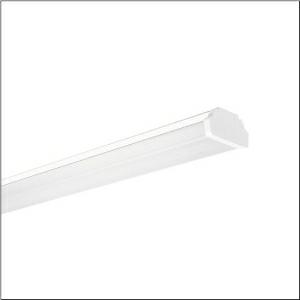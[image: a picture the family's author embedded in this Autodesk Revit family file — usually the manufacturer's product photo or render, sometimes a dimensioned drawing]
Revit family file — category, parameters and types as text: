
# Revit family: dus_r__31_ho_53bd812m1v4120_db1b
name_source: partatom
category: Lighting Fixtures
units: mm (PartAtom-declared; Revit-internal decimal feet)

## family parameters
Cut with Voids When Loaded = No
Host = Face
Light Source = No
Part Type = Normal
Room Calculation Point = No
Round Connector Dimension = Use Diameter
Shared = No

## types (1)
- --- (1 x LED, 12380 lm, 77.3 W, 4000K)
    Apparent Load = 77 VA
    CIE Flux Codes = 47 80 95 92 100
    Color Rendering = 80
    Color Temperature = 4000K
    Default Elevation = 1800 mm
    Description = DUS® 31 HO, luminaire insert, of sheet steel, coil coated, white, length: 1.535mm, width: 81mm, height: 90mm, 5x system unit, system units: 307mm, LED rated luminous flux: 12.380lm, light colour: 840, control gear: ON/OFF Multilumen, control gear: ECG Multilumen, with plug, 3-pole, with phase selection, mains connection: 220..240V, AC, 50/60Hz, rated input power: 77W, through-wiring accessed according to module size, primary optical cover: cover, of PMMA, light emission: direct distribution, primary light characteristic: symmetric, protection rating (complete): IP20, protection rating (LED compartment): IP50, insulation class (complete): insulation class I (protective earthing), certification: CE, ENEC, VDE, UKCA, impact resistance: IK03, permissible ambient temperature for indoor applications: -35..+35°C, corresponds to IFS (International Featured Standards) requirements for safety and quality in the food industry, reducing of maximum allowable ambient temperature of 5°C with ceiling mounting, packaging unit: 1 piece
    Height = 95 mm
    Lamp = 1 x LED
    Lamp Light Flux = 12380 lm
    Lamp Power = 77.3 W
    Lamp count = 1
    Length = 1535 mm
    Luminous efficacy = 160 lm/W
    Manufacturer = Siteco
    ModVariant = No
    Model = 53BD812M1V4120
    Mounting Place = Ceiling
    Mounting Type = Pendant
    Number of Poles = 1
    OnlyDefault = Yes
    Power Factor = 1
    Product Name = DUS® 31 HO
    Product group = luminaire insert
    ProductGroupID = 902
    Protection Class = Protection class I
    Protection Degree = IP 20
    RLX_Detail_Level = 1
    RLX_Emergency_Light_Flux = 0 lm
    RLX_Emergency_Type = 0
    RLX_Emergency_Type_DB = No
    RlxData = <blob elided: 39777 chars, md5=ff79187a>
    Socket = socket
    Standby Power = 0 W
    System Light Flux = 12380 lm
    System Power = 77 W
    Type Comments = factory setting: luminous flux: 100 % | (A | C | E) | 173 mA
    Type Image = l_1319596.jpg
    URL = http://relux.com
    VarID = @adj_199264
    Voltage = 0 V
    Weight = 0.00 kg
    Width = 81 mm

## geometry (parser evidence)
native form markers: Blend x4, Sweep x11
no freeform markers — native parametric forms only
